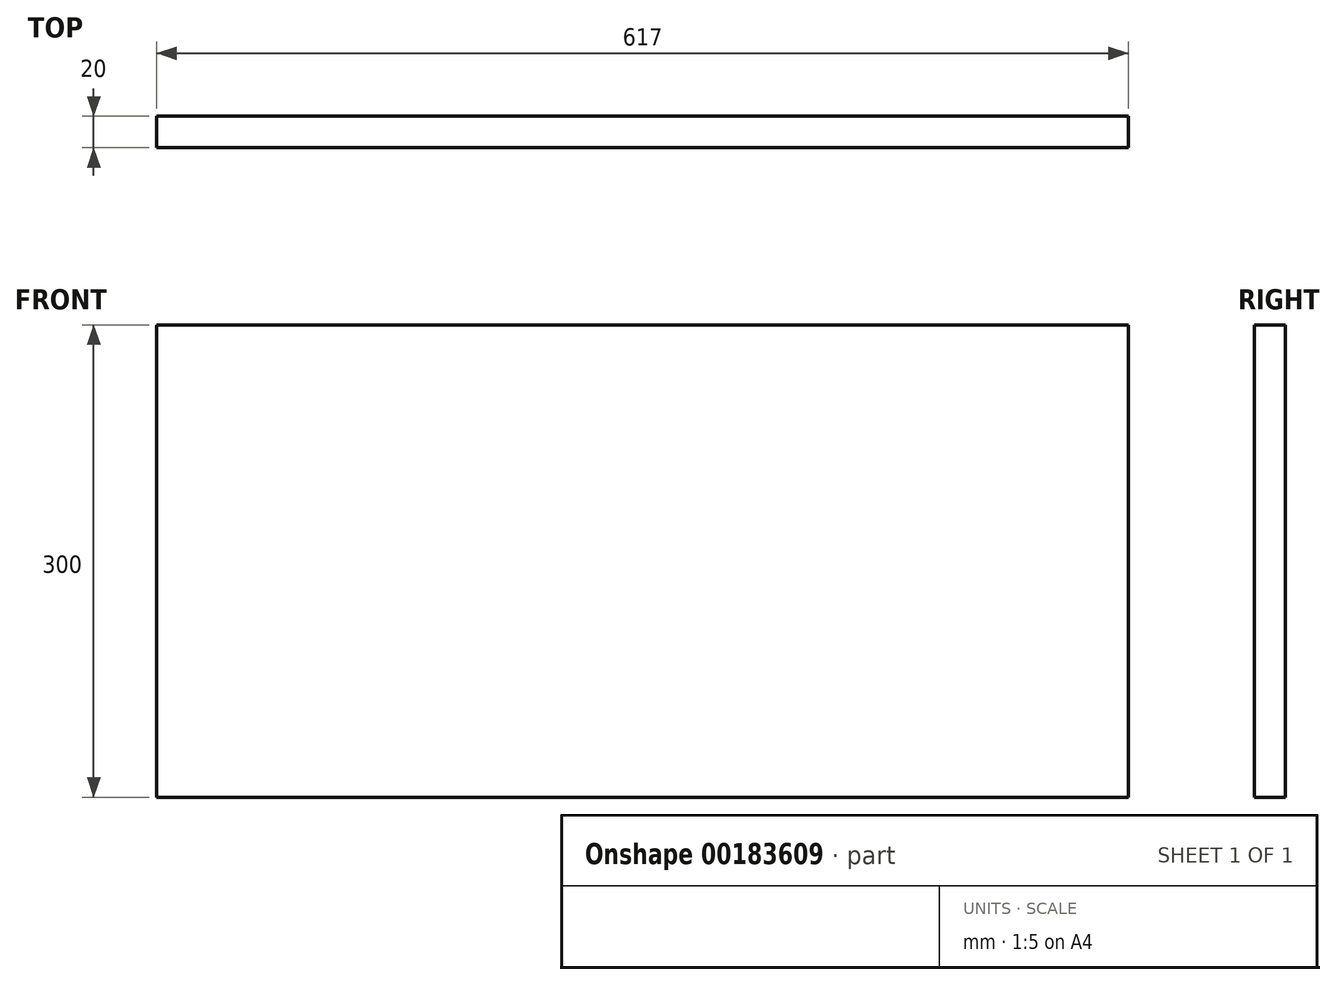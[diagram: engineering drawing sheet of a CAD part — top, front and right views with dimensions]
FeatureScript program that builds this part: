
annotation { "Feature Type Name" : "Feature", "Feature Type Description" : "" }
export const myFeature = defineFeature(function(context is Context, id is Id, definition is map)
    precondition{}
    {
        {
            var Q0;
            Q0=qCreatedBy(makeId("Front.planeOp"),FACE);
            var sketch = newSketch(context, id + "F0", { "sketchPlane" : qUnion([Q0])});
            skLineSegment(sketch, "E0.bottom", {"start": v(308.5, 150) * mm, "end": v(-308.5, 150) * mm});
            skLineSegment(sketch, "E0.top", {"start": v(308.5, -150) * mm, "end": v(-308.5, -150) * mm});
            skLineSegment(sketch, "E0.left", {"start": v(308.5, 150) * mm, "end": v(308.5, -150) * mm});
            skLineSegment(sketch, "E0.right", {"start": v(-308.5, 150) * mm, "end": v(-308.5, -150) * mm});
            skPoint(sketch, "E0.middle", {"position": v(0, 0) * mm});
            skSolve(sketch);
        }
        {
            var Q0;
            Q0 = qSketchRegion(id + "F0", true);
            extrude(context, id + "F1", {"entities" : qUnion([Q0]), "depth" : 20 * mm});
        }
    });
